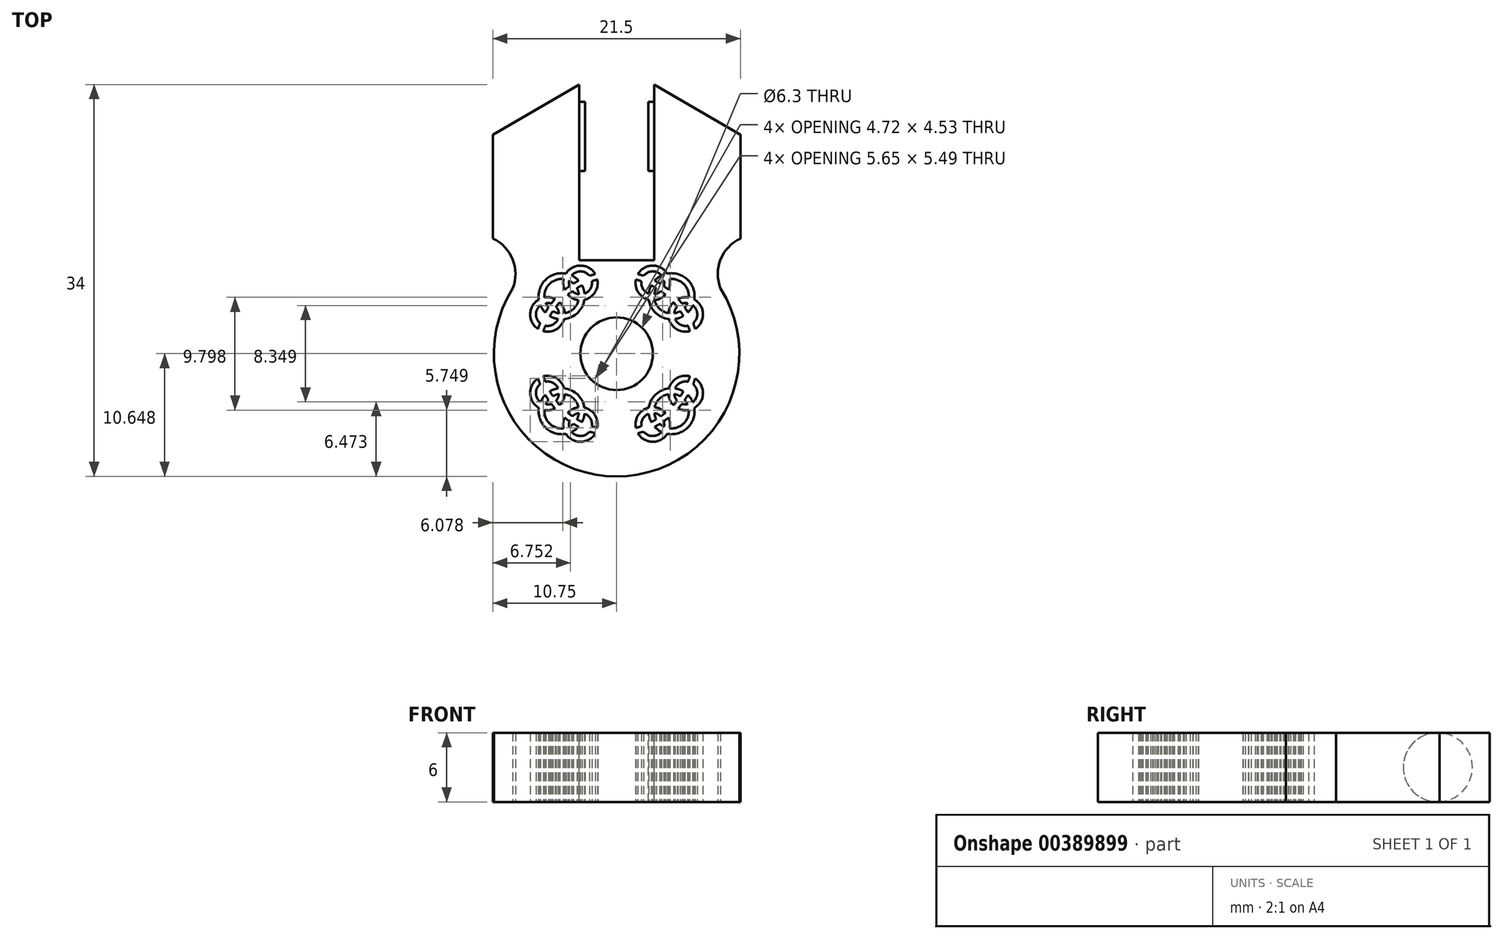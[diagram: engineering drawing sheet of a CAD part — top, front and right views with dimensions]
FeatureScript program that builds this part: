
annotation { "Feature Type Name" : "Feature", "Feature Type Description" : "" }
export const myFeature = defineFeature(function(context is Context, id is Id, definition is map)
    precondition{}
    {
        {
            var Q0;
            Q0=qCreatedBy(makeId("Top.planeOp"),FACE);
            var sketch = newSketch(context, id + "F0", { "sketchPlane" : qUnion([Q0])});
            skArc(sketch, "E0", {"start": v(29.04, 41) * mm, "mid": v(32.3, 20.22) * mm, "end": v(35.54, 41) * mm});
            skCircle(sketch, "E1", {"center": v(32.3, 30.87) * mm, "radius": 3.15 * mm});
            skLineSegment(sketch, "E2", {"start": v(32.3, 38.97) * mm, "end": v(35.54, 38.97) * mm});
            skLineSegment(sketch, "E3", {"start": v(35.54, 38.97) * mm, "end": v(35.54, 54.22) * mm});
            skLineSegment(sketch, "E4", {"start": v(43.04, 49.87) * mm, "end": v(35.54, 54.22) * mm});
            skLineSegment(sketch, "E5", {"start": v(43.04, 49.87) * mm, "end": v(43.04, 40.87) * mm});
            skLineSegment(sketch, "E6.MirrorCS", {"start": v(32.3, 38.97) * mm, "end": v(29.04, 38.97) * mm});
            skLineSegment(sketch, "E7.MirrorCS", {"start": v(29.04, 38.97) * mm, "end": v(29.04, 54.22) * mm});
            skLineSegment(sketch, "E8.MirrorCS", {"start": v(21.54, 49.87) * mm, "end": v(29.04, 54.22) * mm});
            skLineSegment(sketch, "E9.MirrorCS", {"start": v(21.54, 49.87) * mm, "end": v(21.54, 40.87) * mm});
            skArc(sketch, "E10", {"start": v(43.04, 40.87) * mm, "mid": v(41.31, 39.04) * mm, "end": v(41.3, 36.53) * mm});
            skArc(sketch, "E11.MirrorCS", {"start": v(21.54, 40.87) * mm, "mid": v(23.27, 39.04) * mm, "end": v(23.27, 36.53) * mm});
            skArc(sketch, "E12", {"start": v(35.59, 24.52) * mm, "mid": v(35.87, 24.27) * mm, "end": v(36.2, 24.08) * mm});
            skArc(sketch, "E13", {"start": v(37.82, 27.17) * mm, "mid": v(37.57, 27.3) * mm, "end": v(37.3, 27.36) * mm});
            skArc(sketch, "E14", {"start": v(34.14, 23.96) * mm, "mid": v(35.4, 23.22) * mm, "end": v(36.7, 23.92) * mm});
            skArc(sketch, "E15", {"start": v(34.64, 24.11) * mm, "mid": v(35.4, 23.72) * mm, "end": v(36.2, 24.08) * mm});
            skArc(sketch, "E16", {"start": v(38.65, 28.91) * mm, "mid": v(37.54, 28.76) * mm, "end": v(36.85, 27.87) * mm});
            skArc(sketch, "E17", {"start": v(38.48, 28.44) * mm, "mid": v(37.82, 28.34) * mm, "end": v(37.37, 27.86) * mm});
            skArc(sketch, "E18.0", {"start": v(35.59, 24.52) * mm, "mid": v(35.82, 24.65) * mm, "end": v(36.04, 24.78) * mm});
            skArc(sketch, "E19.0", {"start": v(35.3, 24.94) * mm, "mid": v(35.52, 25.05) * mm, "end": v(35.73, 25.18) * mm});
            skArc(sketch, "E20.trimOffspring", {"start": v(34.14, 23.96) * mm, "mid": v(34.39, 24.03) * mm, "end": v(34.64, 24.11) * mm});
            skArc(sketch, "E21.trimOffspring", {"start": v(33.96, 24.43) * mm, "mid": v(34.2, 24.5) * mm, "end": v(34.44, 24.57) * mm});
            skArc(sketch, "E22.trimOffspring", {"start": v(38.08, 27.6) * mm, "mid": v(37.74, 27.76) * mm, "end": v(37.37, 27.86) * mm});
            skArc(sketch, "E23.trimOffspring", {"start": v(38.93, 28.22) * mm, "mid": v(39.03, 28.47) * mm, "end": v(39.1, 28.71) * mm});
            skArc(sketch, "E24.trimOffspring", {"start": v(38.48, 28.44) * mm, "mid": v(38.57, 28.68) * mm, "end": v(38.65, 28.91) * mm});
            skArc(sketch, "E25.trimOffspring", {"start": v(38.2, 26.85) * mm, "mid": v(38.35, 27.07) * mm, "end": v(38.48, 27.29) * mm});
            skArc(sketch, "E26.trimOffspring", {"start": v(37.82, 27.17) * mm, "mid": v(37.95, 27.38) * mm, "end": v(38.08, 27.6) * mm});
            skArc(sketch, "E27.trimOffspring", {"start": v(37.96, 26.51) * mm, "mid": v(38.2, 26.46) * mm, "end": v(38.44, 26.47) * mm});
            skArc(sketch, "E28.trimOffspring", {"start": v(37.63, 26.11) * mm, "mid": v(38.08, 25.97) * mm, "end": v(38.56, 25.98) * mm});
            skArc(sketch, "E29.trimOffspring", {"start": v(36.53, 25.74) * mm, "mid": v(36.1, 26.06) * mm, "end": v(35.6, 26.21) * mm});
            skArc(sketch, "E30.trimOffspring", {"start": v(36.13, 25.44) * mm, "mid": v(35.87, 25.62) * mm, "end": v(35.57, 25.71) * mm});
            skArc(sketch, "E31.trimOffspring", {"start": v(36.04, 24.78) * mm, "mid": v(36.22, 24.64) * mm, "end": v(36.4, 24.53) * mm});
            skArc(sketch, "E32.trimOffspring", {"start": v(37.63, 26.11) * mm, "mid": v(37.8, 26.3) * mm, "end": v(37.96, 26.51) * mm});
            skArc(sketch, "E33.trimOffspring", {"start": v(37.22, 26.4) * mm, "mid": v(37.39, 26.6) * mm, "end": v(37.54, 26.8) * mm});
            skArc(sketch, "E34.trimOffspring", {"start": v(36.13, 25.44) * mm, "mid": v(36.33, 25.59) * mm, "end": v(36.53, 25.74) * mm});
            skArc(sketch, "E35.trimOffspring", {"start": v(36.39, 25) * mm, "mid": v(36.6, 25.16) * mm, "end": v(36.8, 25.32) * mm});
            skArc(sketch, "E36.MirrorCS", {"start": v(37.63, 35.62) * mm, "mid": v(38.08, 35.76) * mm, "end": v(38.56, 35.75) * mm});
            skArc(sketch, "E37.MirrorCS", {"start": v(37.96, 35.22) * mm, "mid": v(38.2, 35.27) * mm, "end": v(38.44, 35.27) * mm});
            skArc(sketch, "E38.trimOffspring", {"start": v(39.04, 26.16) * mm, "mid": v(39.79, 27.42) * mm, "end": v(39.1, 28.71) * mm});
            skArc(sketch, "E39.trimOffspring", {"start": v(38.9, 26.67) * mm, "mid": v(39.29, 27.44) * mm, "end": v(38.93, 28.22) * mm});
            skArc(sketch, "E40.trimOffspring", {"start": v(38.44, 26.47) * mm, "mid": v(38.34, 26.67) * mm, "end": v(38.2, 26.85) * mm});
            skArc(sketch, "E41.trimOffspring", {"start": v(38.9, 26.67) * mm, "mid": v(38.72, 27) * mm, "end": v(38.48, 27.29) * mm});
            skArc(sketch, "E42.trimOffspring", {"start": v(36.8, 27.36) * mm, "mid": v(36.02, 26.97) * mm, "end": v(35.6, 26.21) * mm});
            skArc(sketch, "E43.trimOffspring", {"start": v(37.3, 27.36) * mm, "mid": v(37.37, 27.06) * mm, "end": v(37.54, 26.8) * mm});
            skArc(sketch, "E44.trimOffspring", {"start": v(36.8, 27.36) * mm, "mid": v(36.92, 26.84) * mm, "end": v(37.22, 26.4) * mm});
            skArc(sketch, "E45.trimOffspring", {"start": v(36.85, 27.87) * mm, "mid": v(35.68, 27.33) * mm, "end": v(35.08, 26.18) * mm});
            skArc(sketch, "E46.trimOffspring", {"start": v(35.57, 25.71) * mm, "mid": v(35.63, 25.44) * mm, "end": v(35.73, 25.18) * mm});
            skArc(sketch, "E47.trimOffspring", {"start": v(35.07, 25.66) * mm, "mid": v(35.15, 25.29) * mm, "end": v(35.3, 24.94) * mm});
            skArc(sketch, "E48.trimOffspring", {"start": v(35.07, 25.66) * mm, "mid": v(34.57, 25.23) * mm, "end": v(34.44, 24.57) * mm});
            skArc(sketch, "E49.trimOffspring", {"start": v(35.08, 26.18) * mm, "mid": v(34.17, 25.53) * mm, "end": v(33.96, 24.43) * mm});
            skArc(sketch, "E50.trimOffspring", {"start": v(36.4, 24.53) * mm, "mid": v(36.43, 24.77) * mm, "end": v(36.39, 25) * mm});
            skArc(sketch, "E51.trimOffspring", {"start": v(36.9, 24.4) * mm, "mid": v(36.92, 24.86) * mm, "end": v(36.8, 25.32) * mm});
            skArc(sketch, "E52.trimOffspring", {"start": v(36.9, 24.4) * mm, "mid": v(38.1, 24.8) * mm, "end": v(38.56, 25.98) * mm});
            skArc(sketch, "E53.trimOffspring", {"start": v(36.7, 23.92) * mm, "mid": v(38.44, 24.44) * mm, "end": v(39.04, 26.16) * mm});
            skArc(sketch, "E54.MirrorCS", {"start": v(38.48, 33.3) * mm, "mid": v(38.57, 33.06) * mm, "end": v(38.65, 32.82) * mm});
            skArc(sketch, "E55.MirrorCS", {"start": v(38.93, 33.51) * mm, "mid": v(39.03, 33.27) * mm, "end": v(39.1, 33.02) * mm});
            skArc(sketch, "E56.MirrorCS", {"start": v(38.9, 35.07) * mm, "mid": v(39.29, 34.3) * mm, "end": v(38.93, 33.51) * mm});
            skArc(sketch, "E57.MirrorCS", {"start": v(38.9, 35.07) * mm, "mid": v(38.72, 34.74) * mm, "end": v(38.48, 34.45) * mm});
            skArc(sketch, "E58.MirrorCS", {"start": v(38.2, 34.89) * mm, "mid": v(38.35, 34.67) * mm, "end": v(38.48, 34.45) * mm});
            skArc(sketch, "E59.MirrorCS", {"start": v(37.82, 34.56) * mm, "mid": v(37.95, 34.35) * mm, "end": v(38.08, 34.14) * mm});
            skArc(sketch, "E60.MirrorCS", {"start": v(36.85, 33.87) * mm, "mid": v(35.68, 34.4) * mm, "end": v(35.08, 35.55) * mm});
            skArc(sketch, "E61.MirrorCS", {"start": v(36.7, 37.82) * mm, "mid": v(38.44, 37.3) * mm, "end": v(39.04, 35.58) * mm});
            skArc(sketch, "E62.MirrorCS", {"start": v(36.9, 37.35) * mm, "mid": v(38.1, 36.94) * mm, "end": v(38.56, 35.75) * mm});
            skArc(sketch, "E63.MirrorCS", {"start": v(36.8, 34.38) * mm, "mid": v(36.02, 34.77) * mm, "end": v(35.6, 35.52) * mm});
            skArc(sketch, "E64.MirrorCS", {"start": v(39.04, 35.58) * mm, "mid": v(39.79, 34.32) * mm, "end": v(39.1, 33.02) * mm});
            skArc(sketch, "E65.MirrorCS", {"start": v(38.65, 32.82) * mm, "mid": v(37.54, 32.98) * mm, "end": v(36.85, 33.87) * mm});
            skArc(sketch, "E66.MirrorCS", {"start": v(38.48, 33.3) * mm, "mid": v(37.82, 33.4) * mm, "end": v(37.37, 33.88) * mm});
            skArc(sketch, "E67.MirrorCS", {"start": v(38.08, 34.14) * mm, "mid": v(37.74, 33.97) * mm, "end": v(37.37, 33.88) * mm});
            skArc(sketch, "E68.MirrorCS", {"start": v(37.82, 34.56) * mm, "mid": v(37.57, 34.44) * mm, "end": v(37.3, 34.37) * mm});
            skArc(sketch, "E69.MirrorCS", {"start": v(37.3, 34.37) * mm, "mid": v(37.37, 34.68) * mm, "end": v(37.54, 34.94) * mm});
            skArc(sketch, "E70.MirrorCS", {"start": v(36.8, 34.38) * mm, "mid": v(36.92, 34.9) * mm, "end": v(37.22, 35.33) * mm});
            skArc(sketch, "E71.MirrorCS", {"start": v(37.22, 35.33) * mm, "mid": v(37.39, 35.14) * mm, "end": v(37.54, 34.94) * mm});
            skArc(sketch, "E72.MirrorCS", {"start": v(37.63, 35.62) * mm, "mid": v(37.8, 35.43) * mm, "end": v(37.96, 35.22) * mm});
            skArc(sketch, "E73.MirrorCS", {"start": v(34.64, 37.62) * mm, "mid": v(35.4, 38.01) * mm, "end": v(36.2, 37.66) * mm});
            skArc(sketch, "E74.MirrorCS", {"start": v(35.07, 36.08) * mm, "mid": v(34.57, 36.5) * mm, "end": v(34.44, 37.16) * mm});
            skArc(sketch, "E75.MirrorCS", {"start": v(35.07, 36.08) * mm, "mid": v(35.15, 36.45) * mm, "end": v(35.3, 36.8) * mm});
            skArc(sketch, "E76.MirrorCS", {"start": v(35.08, 35.55) * mm, "mid": v(34.17, 36.2) * mm, "end": v(33.96, 37.3) * mm});
            skArc(sketch, "E77.MirrorCS", {"start": v(34.14, 37.78) * mm, "mid": v(35.4, 38.51) * mm, "end": v(36.7, 37.82) * mm});
            skArc(sketch, "E78.MirrorCS", {"start": v(35.59, 37.21) * mm, "mid": v(35.87, 37.46) * mm, "end": v(36.2, 37.66) * mm});
            skArc(sketch, "E79.MirrorCS", {"start": v(34.14, 37.78) * mm, "mid": v(34.39, 37.7) * mm, "end": v(34.64, 37.62) * mm});
            skArc(sketch, "E80.MirrorCS", {"start": v(33.96, 37.3) * mm, "mid": v(34.2, 37.24) * mm, "end": v(34.44, 37.16) * mm});
            skArc(sketch, "E81.MirrorCS", {"start": v(35.59, 37.21) * mm, "mid": v(35.82, 37.09) * mm, "end": v(36.04, 36.96) * mm});
            skArc(sketch, "E82.MirrorCS", {"start": v(35.3, 36.8) * mm, "mid": v(35.52, 36.68) * mm, "end": v(35.73, 36.56) * mm});
            skArc(sketch, "E83.MirrorCS", {"start": v(36.9, 37.35) * mm, "mid": v(36.92, 36.87) * mm, "end": v(36.8, 36.41) * mm});
            skArc(sketch, "E84.MirrorCS", {"start": v(36.53, 36) * mm, "mid": v(36.1, 35.67) * mm, "end": v(35.6, 35.52) * mm});
            skArc(sketch, "E85.MirrorCS", {"start": v(36.13, 36.3) * mm, "mid": v(35.87, 36.12) * mm, "end": v(35.57, 36.02) * mm});
            skArc(sketch, "E86.MirrorCS", {"start": v(36.39, 36.73) * mm, "mid": v(36.6, 36.57) * mm, "end": v(36.8, 36.41) * mm});
            skArc(sketch, "E87.MirrorCS", {"start": v(36.13, 36.3) * mm, "mid": v(36.33, 36.15) * mm, "end": v(36.53, 36) * mm});
            skArc(sketch, "E88.MirrorCS", {"start": v(38.44, 35.27) * mm, "mid": v(38.34, 35.07) * mm, "end": v(38.2, 34.89) * mm});
            skArc(sketch, "E89.MirrorCS", {"start": v(36.4, 37.2) * mm, "mid": v(36.43, 36.97) * mm, "end": v(36.39, 36.73) * mm});
            skArc(sketch, "E90.MirrorCS", {"start": v(36.04, 36.96) * mm, "mid": v(36.22, 37.1) * mm, "end": v(36.4, 37.2) * mm});
            skArc(sketch, "E91.MirrorCS", {"start": v(35.57, 36.02) * mm, "mid": v(35.63, 36.3) * mm, "end": v(35.73, 36.56) * mm});
            skArc(sketch, "E92.MirrorCS", {"start": v(25.54, 26.16) * mm, "mid": v(24.8, 27.42) * mm, "end": v(25.47, 28.71) * mm});
            skArc(sketch, "E93.MirrorCS", {"start": v(25.93, 28.91) * mm, "mid": v(27.04, 28.76) * mm, "end": v(27.73, 27.87) * mm});
            skArc(sketch, "E94.MirrorCS", {"start": v(25.65, 28.22) * mm, "mid": v(25.56, 28.47) * mm, "end": v(25.47, 28.71) * mm});
            skArc(sketch, "E95.MirrorCS", {"start": v(26.1, 28.44) * mm, "mid": v(26.01, 28.68) * mm, "end": v(25.93, 28.91) * mm});
            skArc(sketch, "E96.MirrorCS", {"start": v(26.1, 28.44) * mm, "mid": v(26.76, 28.34) * mm, "end": v(27.2, 27.86) * mm});
            skArc(sketch, "E97.MirrorCS", {"start": v(25.68, 26.67) * mm, "mid": v(25.3, 27.44) * mm, "end": v(25.65, 28.22) * mm});
            skArc(sketch, "E98.MirrorCS", {"start": v(27.89, 23.92) * mm, "mid": v(26.14, 24.44) * mm, "end": v(25.54, 26.16) * mm});
            skArc(sketch, "E99.MirrorCS", {"start": v(27.69, 24.4) * mm, "mid": v(26.48, 24.8) * mm, "end": v(26.02, 25.98) * mm});
            skArc(sketch, "E100.MirrorCS", {"start": v(25.68, 26.67) * mm, "mid": v(25.86, 27) * mm, "end": v(26.1, 27.29) * mm});
            skArc(sketch, "E101.MirrorCS", {"start": v(26.76, 27.17) * mm, "mid": v(27.01, 27.3) * mm, "end": v(27.29, 27.36) * mm});
            skArc(sketch, "E102.MirrorCS", {"start": v(26.5, 27.6) * mm, "mid": v(26.84, 27.76) * mm, "end": v(27.2, 27.86) * mm});
            skArc(sketch, "E103.MirrorCS", {"start": v(26.76, 27.17) * mm, "mid": v(26.63, 27.38) * mm, "end": v(26.5, 27.6) * mm});
            skArc(sketch, "E104.MirrorCS", {"start": v(28.05, 25.74) * mm, "mid": v(28.48, 26.06) * mm, "end": v(28.98, 26.21) * mm});
            skArc(sketch, "E105.MirrorCS", {"start": v(28.45, 25.44) * mm, "mid": v(28.7, 25.62) * mm, "end": v(29.01, 25.71) * mm});
            skArc(sketch, "E106.MirrorCS", {"start": v(29.01, 25.71) * mm, "mid": v(28.95, 25.44) * mm, "end": v(28.85, 25.18) * mm});
            skArc(sketch, "E107.MirrorCS", {"start": v(29.5, 25.66) * mm, "mid": v(29.43, 25.29) * mm, "end": v(29.28, 24.94) * mm});
            skArc(sketch, "E108.MirrorCS", {"start": v(29.5, 25.66) * mm, "mid": v(30.02, 25.23) * mm, "end": v(30.14, 24.57) * mm});
            skArc(sketch, "E109.MirrorCS", {"start": v(29.5, 26.18) * mm, "mid": v(30.41, 25.53) * mm, "end": v(30.62, 24.43) * mm});
            skArc(sketch, "E110.MirrorCS", {"start": v(30.62, 24.43) * mm, "mid": v(30.38, 24.5) * mm, "end": v(30.14, 24.57) * mm});
            skArc(sketch, "E111.MirrorCS", {"start": v(30.44, 23.96) * mm, "mid": v(30.2, 24.03) * mm, "end": v(29.94, 24.11) * mm});
            skArc(sketch, "E112.MirrorCS", {"start": v(30.44, 23.96) * mm, "mid": v(29.18, 23.22) * mm, "end": v(27.89, 23.92) * mm});
            skArc(sketch, "E113.MirrorCS", {"start": v(29.94, 24.11) * mm, "mid": v(29.17, 23.72) * mm, "end": v(28.39, 24.08) * mm});
            skArc(sketch, "E114.MirrorCS", {"start": v(29, 24.52) * mm, "mid": v(28.7, 24.27) * mm, "end": v(28.39, 24.08) * mm});
            skArc(sketch, "E115.MirrorCS", {"start": v(27.79, 27.36) * mm, "mid": v(28.56, 26.97) * mm, "end": v(28.98, 26.21) * mm});
            skArc(sketch, "E116.MirrorCS", {"start": v(27.73, 27.87) * mm, "mid": v(28.9, 27.33) * mm, "end": v(29.5, 26.18) * mm});
            skArc(sketch, "E117.MirrorCS", {"start": v(26.95, 26.11) * mm, "mid": v(26.5, 25.97) * mm, "end": v(26.02, 25.98) * mm});
            skArc(sketch, "E118.MirrorCS", {"start": v(26.62, 26.51) * mm, "mid": v(26.38, 26.46) * mm, "end": v(26.14, 26.47) * mm});
            skArc(sketch, "E119.MirrorCS", {"start": v(27.36, 26.4) * mm, "mid": v(27.2, 26.6) * mm, "end": v(27.04, 26.8) * mm});
            skArc(sketch, "E120.MirrorCS", {"start": v(28.2, 25) * mm, "mid": v(27.98, 25.16) * mm, "end": v(27.78, 25.32) * mm});
            skArc(sketch, "E121.MirrorCS", {"start": v(28.45, 25.44) * mm, "mid": v(28.25, 25.59) * mm, "end": v(28.05, 25.74) * mm});
            skArc(sketch, "E122.MirrorCS", {"start": v(29.28, 24.94) * mm, "mid": v(29.06, 25.05) * mm, "end": v(28.85, 25.18) * mm});
            skArc(sketch, "E123.MirrorCS", {"start": v(27.29, 27.36) * mm, "mid": v(27.2, 27.06) * mm, "end": v(27.04, 26.8) * mm});
            skArc(sketch, "E124.MirrorCS", {"start": v(27.79, 27.36) * mm, "mid": v(27.66, 26.84) * mm, "end": v(27.36, 26.4) * mm});
            skArc(sketch, "E125.MirrorCS", {"start": v(27.69, 24.4) * mm, "mid": v(27.66, 24.86) * mm, "end": v(27.78, 25.32) * mm});
            skArc(sketch, "E126.MirrorCS", {"start": v(28.17, 24.53) * mm, "mid": v(28.15, 24.77) * mm, "end": v(28.2, 25) * mm});
            skArc(sketch, "E127.MirrorCS", {"start": v(28.54, 24.78) * mm, "mid": v(28.36, 24.64) * mm, "end": v(28.17, 24.53) * mm});
            skArc(sketch, "E128.MirrorCS", {"start": v(29, 24.52) * mm, "mid": v(28.76, 24.65) * mm, "end": v(28.54, 24.78) * mm});
            skArc(sketch, "E129.MirrorCS", {"start": v(26.95, 26.11) * mm, "mid": v(26.78, 26.3) * mm, "end": v(26.62, 26.51) * mm});
            skArc(sketch, "E130.MirrorCS", {"start": v(26.14, 26.47) * mm, "mid": v(26.24, 26.67) * mm, "end": v(26.38, 26.85) * mm});
            skArc(sketch, "E131.MirrorCS", {"start": v(26.38, 26.85) * mm, "mid": v(26.23, 27.07) * mm, "end": v(26.1, 27.29) * mm});
            skArc(sketch, "E132.MirrorCS", {"start": v(25.65, 33.51) * mm, "mid": v(25.56, 33.27) * mm, "end": v(25.47, 33.02) * mm});
            skArc(sketch, "E133.MirrorCS", {"start": v(26.1, 33.3) * mm, "mid": v(26.01, 33.06) * mm, "end": v(25.93, 32.82) * mm});
            skArc(sketch, "E134.MirrorCS", {"start": v(26.1, 33.3) * mm, "mid": v(26.76, 33.4) * mm, "end": v(27.2, 33.88) * mm});
            skArc(sketch, "E135.MirrorCS", {"start": v(25.93, 32.82) * mm, "mid": v(27.04, 32.98) * mm, "end": v(27.73, 33.87) * mm});
            skArc(sketch, "E136.MirrorCS", {"start": v(25.54, 35.58) * mm, "mid": v(24.8, 34.32) * mm, "end": v(25.47, 33.02) * mm});
            skArc(sketch, "E137.MirrorCS", {"start": v(25.68, 35.07) * mm, "mid": v(25.3, 34.3) * mm, "end": v(25.65, 33.51) * mm});
            skArc(sketch, "E138.MirrorCS", {"start": v(25.68, 35.07) * mm, "mid": v(25.86, 34.74) * mm, "end": v(26.1, 34.45) * mm});
            skArc(sketch, "E139.MirrorCS", {"start": v(26.5, 34.14) * mm, "mid": v(26.84, 33.97) * mm, "end": v(27.2, 33.88) * mm});
            skArc(sketch, "E140.MirrorCS", {"start": v(26.76, 34.56) * mm, "mid": v(26.63, 34.35) * mm, "end": v(26.5, 34.14) * mm});
            skArc(sketch, "E141.MirrorCS", {"start": v(26.38, 34.89) * mm, "mid": v(26.23, 34.67) * mm, "end": v(26.1, 34.45) * mm});
            skArc(sketch, "E142.MirrorCS", {"start": v(26.14, 35.27) * mm, "mid": v(26.24, 35.07) * mm, "end": v(26.38, 34.89) * mm});
            skArc(sketch, "E143.MirrorCS", {"start": v(26.76, 34.56) * mm, "mid": v(27.01, 34.44) * mm, "end": v(27.29, 34.37) * mm});
            skArc(sketch, "E144.MirrorCS", {"start": v(27.29, 34.37) * mm, "mid": v(27.2, 34.68) * mm, "end": v(27.04, 34.94) * mm});
            skArc(sketch, "E145.MirrorCS", {"start": v(26.62, 35.22) * mm, "mid": v(26.38, 35.27) * mm, "end": v(26.14, 35.27) * mm});
            skArc(sketch, "E146.MirrorCS", {"start": v(26.95, 35.62) * mm, "mid": v(26.5, 35.76) * mm, "end": v(26.02, 35.75) * mm});
            skArc(sketch, "E147.MirrorCS", {"start": v(27.79, 34.38) * mm, "mid": v(27.66, 34.9) * mm, "end": v(27.36, 35.33) * mm});
            skArc(sketch, "E148.MirrorCS", {"start": v(26.95, 35.62) * mm, "mid": v(26.78, 35.43) * mm, "end": v(26.62, 35.22) * mm});
            skArc(sketch, "E149.MirrorCS", {"start": v(27.36, 35.33) * mm, "mid": v(27.2, 35.14) * mm, "end": v(27.04, 34.94) * mm});
            skArc(sketch, "E150.MirrorCS", {"start": v(27.89, 37.82) * mm, "mid": v(26.14, 37.3) * mm, "end": v(25.54, 35.58) * mm});
            skArc(sketch, "E151.MirrorCS", {"start": v(27.69, 37.35) * mm, "mid": v(26.48, 36.94) * mm, "end": v(26.02, 35.75) * mm});
            skArc(sketch, "E152.MirrorCS", {"start": v(27.79, 34.38) * mm, "mid": v(28.56, 34.77) * mm, "end": v(28.98, 35.52) * mm});
            skArc(sketch, "E153.MirrorCS", {"start": v(27.73, 33.87) * mm, "mid": v(28.9, 34.4) * mm, "end": v(29.5, 35.55) * mm});
            skArc(sketch, "E154.MirrorCS", {"start": v(28.05, 36) * mm, "mid": v(28.48, 35.67) * mm, "end": v(28.98, 35.52) * mm});
            skArc(sketch, "E155.MirrorCS", {"start": v(27.69, 37.35) * mm, "mid": v(27.66, 36.87) * mm, "end": v(27.78, 36.41) * mm});
            skArc(sketch, "E156.MirrorCS", {"start": v(28.2, 36.73) * mm, "mid": v(27.98, 36.57) * mm, "end": v(27.78, 36.41) * mm});
            skArc(sketch, "E157.MirrorCS", {"start": v(28.45, 36.3) * mm, "mid": v(28.25, 36.15) * mm, "end": v(28.05, 36) * mm});
            skArc(sketch, "E158.MirrorCS", {"start": v(28.45, 36.3) * mm, "mid": v(28.7, 36.12) * mm, "end": v(29.01, 36.02) * mm});
            skArc(sketch, "E159.MirrorCS", {"start": v(28.17, 37.2) * mm, "mid": v(28.15, 36.97) * mm, "end": v(28.2, 36.73) * mm});
            skArc(sketch, "E160.MirrorCS", {"start": v(28.54, 36.96) * mm, "mid": v(28.36, 37.1) * mm, "end": v(28.17, 37.2) * mm});
            skArc(sketch, "E161.MirrorCS", {"start": v(29.5, 35.55) * mm, "mid": v(30.41, 36.2) * mm, "end": v(30.62, 37.3) * mm});
            skArc(sketch, "E162.MirrorCS", {"start": v(29.5, 36.08) * mm, "mid": v(30.02, 36.5) * mm, "end": v(30.14, 37.16) * mm});
            skArc(sketch, "E163.MirrorCS", {"start": v(29.5, 36.08) * mm, "mid": v(29.43, 36.45) * mm, "end": v(29.28, 36.8) * mm});
            skArc(sketch, "E164.MirrorCS", {"start": v(29.01, 36.02) * mm, "mid": v(28.95, 36.3) * mm, "end": v(28.85, 36.56) * mm});
            skArc(sketch, "E165.MirrorCS", {"start": v(29.28, 36.8) * mm, "mid": v(29.06, 36.68) * mm, "end": v(28.85, 36.56) * mm});
            skArc(sketch, "E166.MirrorCS", {"start": v(29, 37.21) * mm, "mid": v(28.76, 37.09) * mm, "end": v(28.54, 36.96) * mm});
            skArc(sketch, "E167.MirrorCS", {"start": v(29, 37.21) * mm, "mid": v(28.7, 37.46) * mm, "end": v(28.39, 37.66) * mm});
            skArc(sketch, "E168.MirrorCS", {"start": v(30.44, 37.78) * mm, "mid": v(29.18, 38.51) * mm, "end": v(27.89, 37.82) * mm});
            skArc(sketch, "E169.MirrorCS", {"start": v(29.94, 37.62) * mm, "mid": v(29.17, 38.01) * mm, "end": v(28.39, 37.66) * mm});
            skArc(sketch, "E170.MirrorCS", {"start": v(30.44, 37.78) * mm, "mid": v(30.2, 37.7) * mm, "end": v(29.94, 37.62) * mm});
            skArc(sketch, "E171.MirrorCS", {"start": v(30.62, 37.3) * mm, "mid": v(30.38, 37.24) * mm, "end": v(30.14, 37.16) * mm});
            skSolve(sketch);
        }
        {
            var Q0;
            Q0 = qSketchRegion(id + "F0", true);
            extrude(context, id + "F1", {"entities" : qUnion([Q0]), "depth" : 6 * mm});
        }
        {
            var Q0;
            Q0=qCreatedBy(makeId("Right.planeOp"),FACE);
            var sketch = newSketch(context, id + "F2", { "sketchPlane" : qUnion([Q0])});
            skCircle(sketch, "E172", {"center": v(49.72, 3) * mm, "radius": 3 * mm});
            skSolve(sketch);
        }
        {
            var Q0;
            Q0 = qSketchRegion(id + "F2", true);
            extrude(context, id + "F3", {"entities" : qUnion([Q0]), "operationType" : NewBodyOperationType.ADD, "depth" : 36.6 * mm, "hasSecondDirection" : true, "secondDirectionOppositeDirection" : false, "secondDirectionDepth" : 27.9 * mm});
        }
        {
            var Q0;
            Q0=qCreatedBy(makeId("Top.planeOp"),FACE);
            var sketch = newSketch(context, id + "F4", { "sketchPlane" : qUnion([Q0])});
            skLineSegment(sketch, "E173", {"start": v(29.54, 49.5) * mm, "end": v(29.54, 54.14) * mm});
            skLineSegment(sketch, "E174", {"start": v(29.54, 54.14) * mm, "end": v(35.04, 54.14) * mm});
            skLineSegment(sketch, "E175", {"start": v(35.04, 54.14) * mm, "end": v(35.04, 45.95) * mm});
            skLineSegment(sketch, "E176", {"start": v(35.04, 45.95) * mm, "end": v(29.54, 45.95) * mm});
            skLineSegment(sketch, "E177", {"start": v(29.54, 45.95) * mm, "end": v(29.54, 49.5) * mm});
            skPoint(sketch, "E178.end.orphan", {"position": v(35.04, 50.08) * mm});
            skSolve(sketch);
        }
        {
            var Q0;
            Q0 = qSketchRegion(id + "F4", true);
            extrude(context, id + "F5", {"entities" : qUnion([Q0]), "operationType" : NewBodyOperationType.REMOVE, "depth" : 19 * mm, "hasSecondDirection" : true, "secondDirectionOppositeDirection" : true, "secondDirectionDepth" : 25 * mm});
        }
    });
